# Revit family: Screen-Desk_Mounted-Teknion-JNSEEW-Felt_Elevated-R2018
name_source: partatom
category: Furniture
revit_build: Autodesk Revit 2018 (Build: 20190510_1515(x64)
units: mm (PartAtom-declared; Revit-internal decimal feet)

## family parameters
Always vertical = Yes
Cut with Voids When Loaded = No
OmniClass Number = 23.40.20.00
OmniClass Title = General Furniture and Specialties
Room Calculation Point = No
Shared = Yes
Work Plane-Based = No

## types (3) — shared parameters
Assembly Code = E2020200
Available Heights = 42, 51, or 57 inches.
Manufacturer = Teknion
Manufacturer Fax = 416.661.4586
Part Number = JNSEEW
Product Documentation Link = http://www.teknion.com
Product Line = Expansion Cityline
Product Page URL = http://www.teknion.com
Series = Expansion Cityline
Sustainability Data = http://www.teknion.com
URL = www.teknion.com
Unit Weight URL = http://www.teknion.com
Warranty = http://www.teknion.com

## per-type parameters (varying)
| type | Description | Left Worksurface Bracket | Model | Right Worksurface Bracket |
| Has Worksurface Only Mounting Style | Felt Elevated Screen – Worksurface-Mounted, Worksurface Only Mounting Style, 10" from Floor Modesty Base Height, Standard Width Extension for Corner Application, Radius Corner Detail | Yes | JNSEEWW10____SR | Yes |
| Support Connection on Left Mounting Style | Felt Elevated Screen – Worksurface-Mounted, Support Connection on Left Mounting Style, 10" from Floor Modesty Base Height, Standard Width Extension for Corner Application, Radius Corner Detail | No | JNSEEWL10____SR | Yes |
| Support Connection on Right Mounting Style | Felt Elevated Screen – Worksurface-Mounted, Support Connection on Right Mounting Style, 10" from Floor Modesty Base Height, Standard Width Extension for Corner Application, Radius Corner Detail | Yes | JNSEEWR10____SR | No |

type visibility flags: 3 boolean params named "<type name>" — each type sets only its own to Yes (folded from table)

## geometry (parser evidence)
native form markers: Blend x2, Sweep x2
no freeform markers — native parametric forms only
